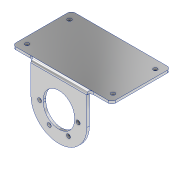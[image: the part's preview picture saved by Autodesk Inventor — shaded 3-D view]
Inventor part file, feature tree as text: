
AUTODESK INVENTOR PART (.ipt)
format: ipt  version: 2022 (Build 260153000, 153)  size: 221,184 bytes
history: native  units: mm
features: sketch x6, extrude x3, sheet_metal_op x2, hole x2, fillet x1, other x1, projected_geometry x1
ambient origin geometry x8: Origin, YZ Plane, XZ Plane, XY Plane, X Axis, Y Axis, Z Axis, Center Point
bodies: Solid1 (feature_tree)
feature tree (16):
  extrude  "Extrusion1"  Depth=6.5mm
  sheet_metal_op  "Face1"
  extrude  "Extrusion3"  Depth=45.0mm
  hole  "Hole1"  [1 undecoded]
  hole  "Hole2"  [1 undecoded]
  extrude  "Extrusion2"  Depth=2.0mm
  fillet  "Fillet2"  Radius=31.0mm
  sketch  "Sketch1"  dims[d1=37.0mm d3=6.5mm]
  sketch  "Sketch2"  dims[d4=50.0mm d5=45.0mm]
  other  "Plate1"
  sheet_metal_op  "Bend1"
  sketch  "Sketch3"  dims[d6=2.0mm d7=0.0mm d8=2.0mm]
  sketch  "Sketch4"  dims[d9=0.5mm d10=2.0mm d11=1.0mm]
  sketch  "Sketch6"  dims[d12=4.0mm d13=2.0mm d14=31.0mm]
  sketch  "Sketch8"  dims[d15=30.0mm d17=360.0deg d19=3.2mm d20=6.0mm d21=4.0mm d22=2.0mm d23=90.0deg d24=2.0mm d25=20.594885mm d26=34.0mm d27=69.0mm d28=3.2mm d29=6.0mm d30=4.0mm d31=2.0mm d32=90.0deg d33=8.0mm d34=20.594885mm d36=7.0mm d45=25.0mm d46=2.0mm d47=0.0mm d48=0.0mm d50=80.0mm d51=10.0mm d52=0.0mm d53=3.0mm]
  projected_geometry  "Project Cut Edges1"
note: 2 required parameter values undecoded (feature->parameter linkage not recoverable at this tier; creation-order binding heuristic only, values carry confidence <= 0.55)
